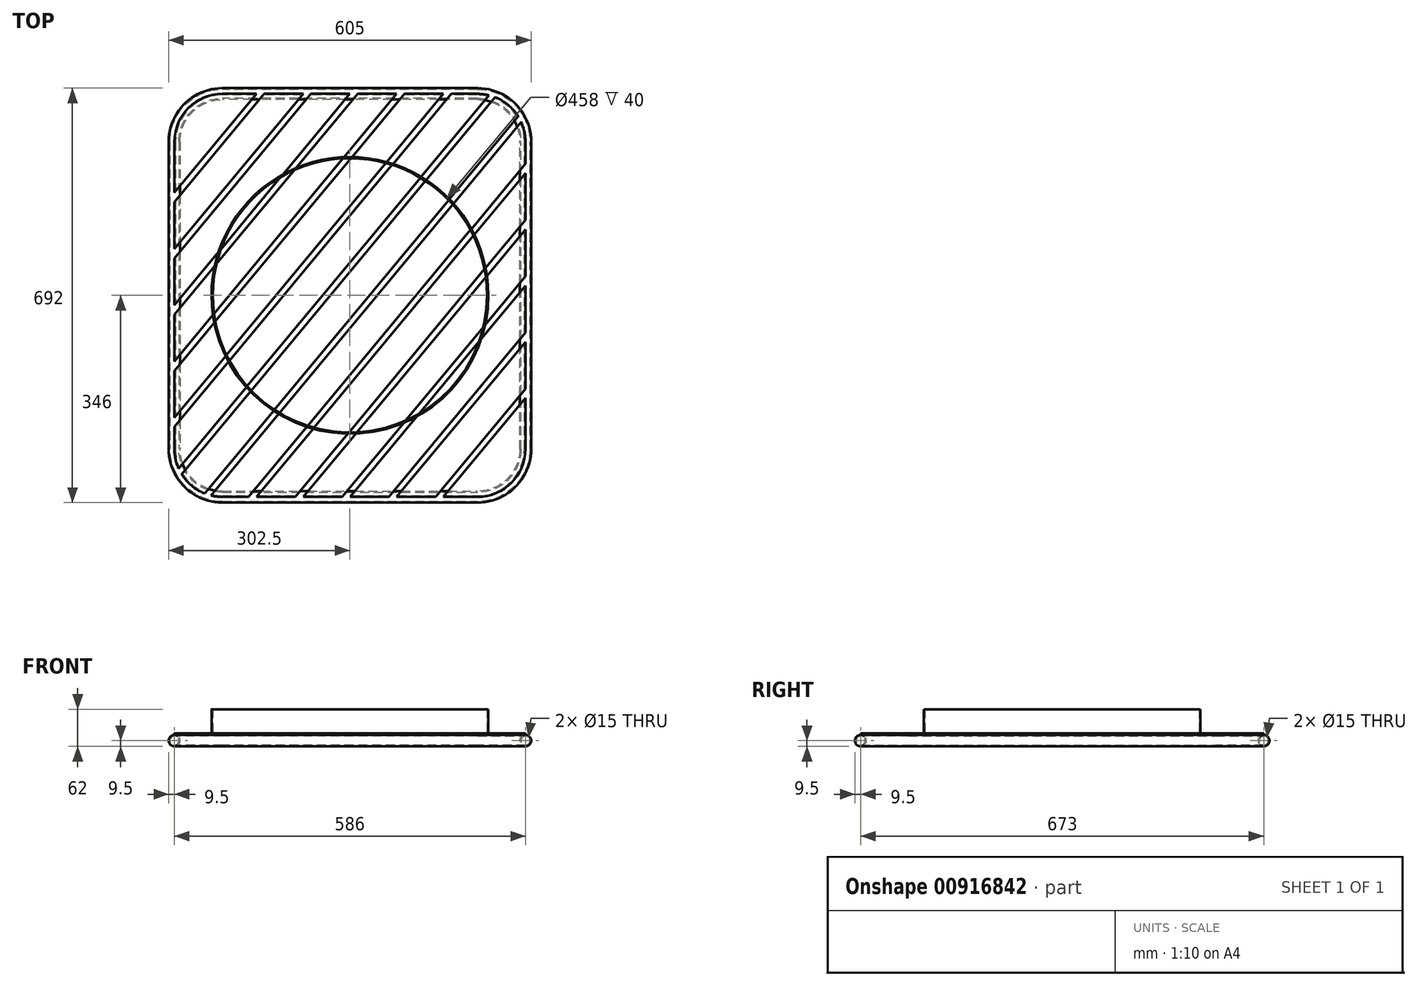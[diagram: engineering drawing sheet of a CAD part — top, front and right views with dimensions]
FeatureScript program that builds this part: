
annotation { "Feature Type Name" : "Feature", "Feature Type Description" : "" }
export const myFeature = defineFeature(function(context is Context, id is Id, definition is map)
    precondition{}
    {
        {
            var Q0;
            Q0=qCreatedBy(makeId("Top.planeOp"),FACE);
            var sketch = newSketch(context, id + "F0", { "sketchPlane" : qUnion([Q0])});
            skLineSegment(sketch, "E0.bottom", {"start": v(-213, 336.5) * mm, "end": v(213, 336.5) * mm});
            skLineSegment(sketch, "E0.top", {"start": v(-213, -336.5) * mm, "end": v(213, -336.5) * mm});
            skLineSegment(sketch, "E0.left", {"start": v(-293, 256.5) * mm, "end": v(-293, -256.5) * mm});
            skLineSegment(sketch, "E0.right", {"start": v(293, 256.5) * mm, "end": v(293, -256.5) * mm});
            skPoint(sketch, "E0.middle", {"position": v(0, 0) * mm});
            skArc(sketch, "E1", {"start": v(-213, 336.5) * mm, "mid": v(-269.57, 313.07) * mm, "end": v(-293, 256.5) * mm});
            skArc(sketch, "E2", {"start": v(293, 256.5) * mm, "mid": v(269.57, 313.07) * mm, "end": v(213, 336.5) * mm});
            skPoint(sketch, "E3.orphan", {"position": v(-293, 336.5) * mm});
            skPoint(sketch, "E4.orphan", {"position": v(293, 336.5) * mm});
            skArc(sketch, "E5.MirrorCS", {"start": v(293, -256.5) * mm, "mid": v(269.57, -313.07) * mm, "end": v(213, -336.5) * mm});
            skArc(sketch, "E6.MirrorCS", {"start": v(-213, -336.5) * mm, "mid": v(-269.57, -313.07) * mm, "end": v(-293, -256.5) * mm});
            skPoint(sketch, "E7.orphan", {"position": v(-293, -336.5) * mm});
            skPoint(sketch, "E8.orphan", {"position": v(293, -336.5) * mm});
            skSolve(sketch);
        }
        {
            var Q0;
            Q0=qCreatedBy(makeId("Front.planeOp"),FACE);
            var sketch = newSketch(context, id + "F1", { "sketchPlane" : qUnion([Q0])});
            skCircle(sketch, "E9", {"center": v(-293, 0) * mm, "radius": 9.5 * mm});
            skCircle(sketch, "E10", {"center": v(-293, 0) * mm, "radius": 7.5 * mm});
            skSolve(sketch);
        }
        {
            var Q0;
            Q0=makeQuery(id+"F1.imprint","IMPRINT",FACE,{"disambiguationData":[TD([[makeQuery(id+"F1.imprint","IMPRINT",EDGE,{"derivedFrom":sQuery(id+"F1.wireOp",EDGE,"E9")}),1.0]])]});
            var Q1;
            Q1=sQuery(id+"F0.wireOp",EDGE,"E0.left");
            var Q2;
            Q2=sQuery(id+"F0.wireOp",EDGE,"E1");
            var Q3;
            Q3=sQuery(id+"F0.wireOp",EDGE,"E0.bottom");
            var Q4;
            Q4=sQuery(id+"F0.wireOp",EDGE,"E2");
            var Q5;
            Q5=sQuery(id+"F0.wireOp",EDGE,"E0.right");
            var Q6;
            Q6=sQuery(id+"F0.wireOp",EDGE,"E5.MirrorCS");
            var Q7;
            Q7=sQuery(id+"F0.wireOp",EDGE,"E0.top");
            var Q8;
            Q8=sQuery(id+"F0.wireOp",EDGE,"E6.MirrorCS");
            sweep(context, id + "F2", {"profiles" : qUnion([Q0]), "path" : qUnion([Q1, Q2, Q3, Q4, Q5, Q6, Q7, Q8])});
        }
        {
            var Q0;
            Q0=qCreatedBy(makeId("Top.planeOp"),FACE);
            cPlane(context, id + "F3", {"entities" : qUnion([Q0]), "cplaneType" : CPlaneType.OFFSET, "offset" : 9.5 * mm, "width" : 150 * mm, "height" : 150 * mm});
        }
        {
            var Q0;
            Q0=qCreatedBy(id+"F3.planeOp",FACE);
            var sketch = newSketch(context, id + "F4", { "sketchPlane" : qUnion([Q0])});
            skLineSegment(sketch, "E11.bottom", {"start": v(-213, 336.5) * mm, "end": v(213, 336.5) * mm});
            skLineSegment(sketch, "E11.top", {"start": v(-213, -336.5) * mm, "end": v(213, -336.5) * mm});
            skLineSegment(sketch, "E11.left", {"start": v(-293, 256.5) * mm, "end": v(-293, -256.5) * mm});
            skLineSegment(sketch, "E11.right", {"start": v(293, 256.5) * mm, "end": v(293, -256.5) * mm});
            skPoint(sketch, "E11.middle", {"position": v(0, 0) * mm});
            skArc(sketch, "E12", {"start": v(293, 256.5) * mm, "mid": v(269.57, 313.07) * mm, "end": v(213, 336.5) * mm});
            skArc(sketch, "E13", {"start": v(-213, 336.5) * mm, "mid": v(-269.57, 313.07) * mm, "end": v(-293, 256.5) * mm});
            skPoint(sketch, "E14.orphan", {"position": v(293, 336.5) * mm});
            skPoint(sketch, "E15.orphan", {"position": v(-293, 336.5) * mm});
            skArc(sketch, "E16.MirrorCS", {"start": v(-213, -336.5) * mm, "mid": v(-269.57, -313.07) * mm, "end": v(-293, -256.5) * mm});
            skArc(sketch, "E17.MirrorCS", {"start": v(293, -256.5) * mm, "mid": v(269.57, -313.07) * mm, "end": v(213, -336.5) * mm});
            skPoint(sketch, "E18.orphan", {"position": v(-293, -336.5) * mm});
            skPoint(sketch, "E19.orphan", {"position": v(293, -336.5) * mm});
            skLineSegment(sketch, "E20", {"start": v(242.32, 330.94) * mm, "end": v(-280.78, -299) * mm});
            skLineSegment(sketch, "E21", {"start": v(-242.32, -330.94) * mm, "end": v(280.78, 299) * mm});
            skLineSegment(sketch, "E22", {"start": v(285.88, 289.48) * mm, "end": v(-232.03, -334.2) * mm});
            skLineSegment(sketch, "E23", {"start": v(-168.95, -336.5) * mm, "end": v(293, 219.79) * mm});
            skLineSegment(sketch, "E24", {"start": v(293, 204.13) * mm, "end": v(-155.95, -336.5) * mm});
            skLineSegment(sketch, "E25", {"start": v(-90.96, -336.5) * mm, "end": v(293, 125.87) * mm});
            skLineSegment(sketch, "E26", {"start": v(293, 110.22) * mm, "end": v(-77.96, -336.5) * mm});
            skLineSegment(sketch, "E27", {"start": v(-12.97, -336.5) * mm, "end": v(293, 31.95) * mm});
            skLineSegment(sketch, "E28", {"start": v(293, 16.3) * mm, "end": v(0.03, -336.5) * mm});
            skLineSegment(sketch, "E29", {"start": v(293, -61.97) * mm, "end": v(65.02, -336.5) * mm});
            skLineSegment(sketch, "E30", {"start": v(293, -77.62) * mm, "end": v(78.02, -336.5) * mm});
            skLineSegment(sketch, "E31", {"start": v(293, -155.88) * mm, "end": v(143.01, -336.5) * mm});
            skLineSegment(sketch, "E32", {"start": v(293, -171.54) * mm, "end": v(156.01, -336.5) * mm});
            skLineSegment(sketch, "E33", {"start": v(292.74, -250.1) * mm, "end": v(221.37, -336.06) * mm});
            skLineSegment(sketch, "E34", {"start": v(232.03, 334.2) * mm, "end": v(-285.88, -289.48) * mm});
            skLineSegment(sketch, "E35", {"start": v(168.95, 336.5) * mm, "end": v(-293, -219.79) * mm});
            skLineSegment(sketch, "E36", {"start": v(-293, -204.13) * mm, "end": v(155.95, 336.5) * mm});
            skLineSegment(sketch, "E37", {"start": v(90.96, 336.5) * mm, "end": v(-293, -125.87) * mm});
            skLineSegment(sketch, "E38", {"start": v(-293, -110.22) * mm, "end": v(77.96, 336.5) * mm});
            skLineSegment(sketch, "E39", {"start": v(12.97, 336.5) * mm, "end": v(-293, -31.95) * mm});
            skLineSegment(sketch, "E40", {"start": v(-293, -16.3) * mm, "end": v(-0.03, 336.5) * mm});
            skLineSegment(sketch, "E41", {"start": v(-65.02, 336.5) * mm, "end": v(-293, 61.97) * mm});
            skLineSegment(sketch, "E42", {"start": v(-293, 77.62) * mm, "end": v(-78.02, 336.5) * mm});
            skLineSegment(sketch, "E43", {"start": v(-143.01, 336.5) * mm, "end": v(-293, 155.88) * mm});
            skLineSegment(sketch, "E44", {"start": v(-221.37, 336.06) * mm, "end": v(-292.74, 250.1) * mm});
            skLineSegment(sketch, "E45", {"start": v(-156.01, 336.5) * mm, "end": v(-293, 171.54) * mm});
            skLineSegment(sketch, "E46", {"start": v(-213, -256.5) * mm, "end": v(213, 256.5) * mm});
            skSolve(sketch);
        }
        {
            var Q0;
            {var subQ3=sQuery(id+"F4.wireOp",EDGE,"E44");Q0=makeQuery(id+"F4.imprint","IMPRINT",FACE,{"disambiguationData":[TD([[makeQuery(id+"F4.imprint","IMPRINT",EDGE,{"derivedFrom":subQ3}),1.0]])]});}
            var Q1;
            {var subQ0=sQuery(id+"F4.wireOp",EDGE,"E42");Q1=makeQuery(id+"F4.imprint","IMPRINT",FACE,{"disambiguationData":[TD([[makeQuery(id+"F4.imprint","IMPRINT",EDGE,{"derivedFrom":subQ0}),1.0]])]});}
            var Q2;
            {var subQ0=sQuery(id+"F4.wireOp",EDGE,"E40");Q2=makeQuery(id+"F4.imprint","IMPRINT",FACE,{"disambiguationData":[TD([[makeQuery(id+"F4.imprint","IMPRINT",EDGE,{"derivedFrom":subQ0}),1.0]])]});}
            var Q3;
            {var subQ0=sQuery(id+"F4.wireOp",EDGE,"E38");Q3=makeQuery(id+"F4.imprint","IMPRINT",FACE,{"disambiguationData":[TD([[makeQuery(id+"F4.imprint","IMPRINT",EDGE,{"derivedFrom":subQ0}),1.0]])]});}
            var Q4;
            {var subQ0=sQuery(id+"F4.wireOp",EDGE,"E36");Q4=makeQuery(id+"F4.imprint","IMPRINT",FACE,{"disambiguationData":[TD([[makeQuery(id+"F4.imprint","IMPRINT",EDGE,{"derivedFrom":subQ0}),1.0]])]});}
            var Q5;
            {var subQ3=sQuery(id+"F4.wireOp",EDGE,"E34");Q5=makeQuery(id+"F4.imprint","IMPRINT",FACE,{"disambiguationData":[TD([[makeQuery(id+"F4.imprint","IMPRINT",EDGE,{"derivedFrom":subQ3}),-1.0]])]});}
            var Q6;
            Q6=makeQuery(id+"F4.imprint","IMPRINT",FACE,{"disambiguationData":[TD([[makeQuery(id+"F4.imprint","IMPRINT",EDGE,{"derivedFrom":sQuery(id+"F4.wireOp",EDGE,"E20")}),1.0]])]});
            var Q7;
            {var subQ3=sQuery(id+"F4.wireOp",EDGE,"E22");Q7=makeQuery(id+"F4.imprint","IMPRINT",FACE,{"disambiguationData":[TD([[makeQuery(id+"F4.imprint","IMPRINT",EDGE,{"derivedFrom":subQ3}),1.0]])]});}
            var Q8;
            {var subQ0=sQuery(id+"F4.wireOp",EDGE,"E24");Q8=makeQuery(id+"F4.imprint","IMPRINT",FACE,{"disambiguationData":[TD([[makeQuery(id+"F4.imprint","IMPRINT",EDGE,{"derivedFrom":subQ0}),1.0]])]});}
            var Q9;
            {var subQ0=sQuery(id+"F4.wireOp",EDGE,"E26");Q9=makeQuery(id+"F4.imprint","IMPRINT",FACE,{"disambiguationData":[TD([[makeQuery(id+"F4.imprint","IMPRINT",EDGE,{"derivedFrom":subQ0}),1.0]])]});}
            var Q10;
            {var subQ0=sQuery(id+"F4.wireOp",EDGE,"E28");Q10=makeQuery(id+"F4.imprint","IMPRINT",FACE,{"disambiguationData":[TD([[makeQuery(id+"F4.imprint","IMPRINT",EDGE,{"derivedFrom":subQ0}),1.0]])]});}
            var Q11;
            {var subQ0=sQuery(id+"F4.wireOp",EDGE,"E30");Q11=makeQuery(id+"F4.imprint","IMPRINT",FACE,{"disambiguationData":[TD([[makeQuery(id+"F4.imprint","IMPRINT",EDGE,{"derivedFrom":subQ0}),1.0]])]});}
            var Q12;
            {var subQ6=sQuery(id+"F4.wireOp",EDGE,"E45");Q12=makeQuery(id+"F4.imprint","IMPRINT",FACE,{"disambiguationData":[TD([[makeQuery(id+"F4.imprint","IMPRINT",EDGE,{"derivedFrom":subQ6}),-1.0]])]});}
            var Q13;
            {var subQ6=sQuery(id+"F4.wireOp",EDGE,"E32");Q13=makeQuery(id+"F4.imprint","IMPRINT",FACE,{"disambiguationData":[TD([[makeQuery(id+"F4.imprint","IMPRINT",EDGE,{"derivedFrom":subQ6}),1.0]])]});}
            extrude(context, id + "F5", {"entities" : qUnion([Q0, Q1, Q2, Q3, Q4, Q5, Q6, Q7, Q8, Q9, Q10, Q11, Q12, Q13]), "operationType" : NewBodyOperationType.ADD, "depth" : 3 * mm, "offsetDistance" : 25 * mm, "hasSecondDirection" : true, "secondDirectionOppositeDirection" : true, "secondDirectionDepth" : .2 * mm});
        }
        {
            var Q0;
            Q0=makeQuery(id+"F5.opExtrude","CAP_FACE",FACE,{"disambiguationData":[OSD([sQuery(id+"F4.wireOp",EDGE,"E11.bottom"),sQuery(id+"F4.wireOp",EDGE,"E11.left"),sQuery(id+"F4.wireOp",EDGE,"E36"),sQuery(id+"F4.wireOp",EDGE,"E37")])],"isStart":false});
            var sketch = newSketch(context, id + "F6", { "sketchPlane" : qUnion([Q0])});
            skCircle(sketch, "E47", {"center": v(0, 0) * mm, "radius": 229 * mm});
            skCircle(sketch, "E48", {"center": v(0, 0) * mm, "radius": 231 * mm});
            skSolve(sketch);
        }
        {
            var Q0;
            Q0=qSketchRegion(id+"F6",true);
            extrude(context, id + "F7", {"entities" : qUnion([Q0]), "operationType" : NewBodyOperationType.ADD, "depth" : 40 * mm, "offsetDistance" : 25 * mm});
        }
    });
